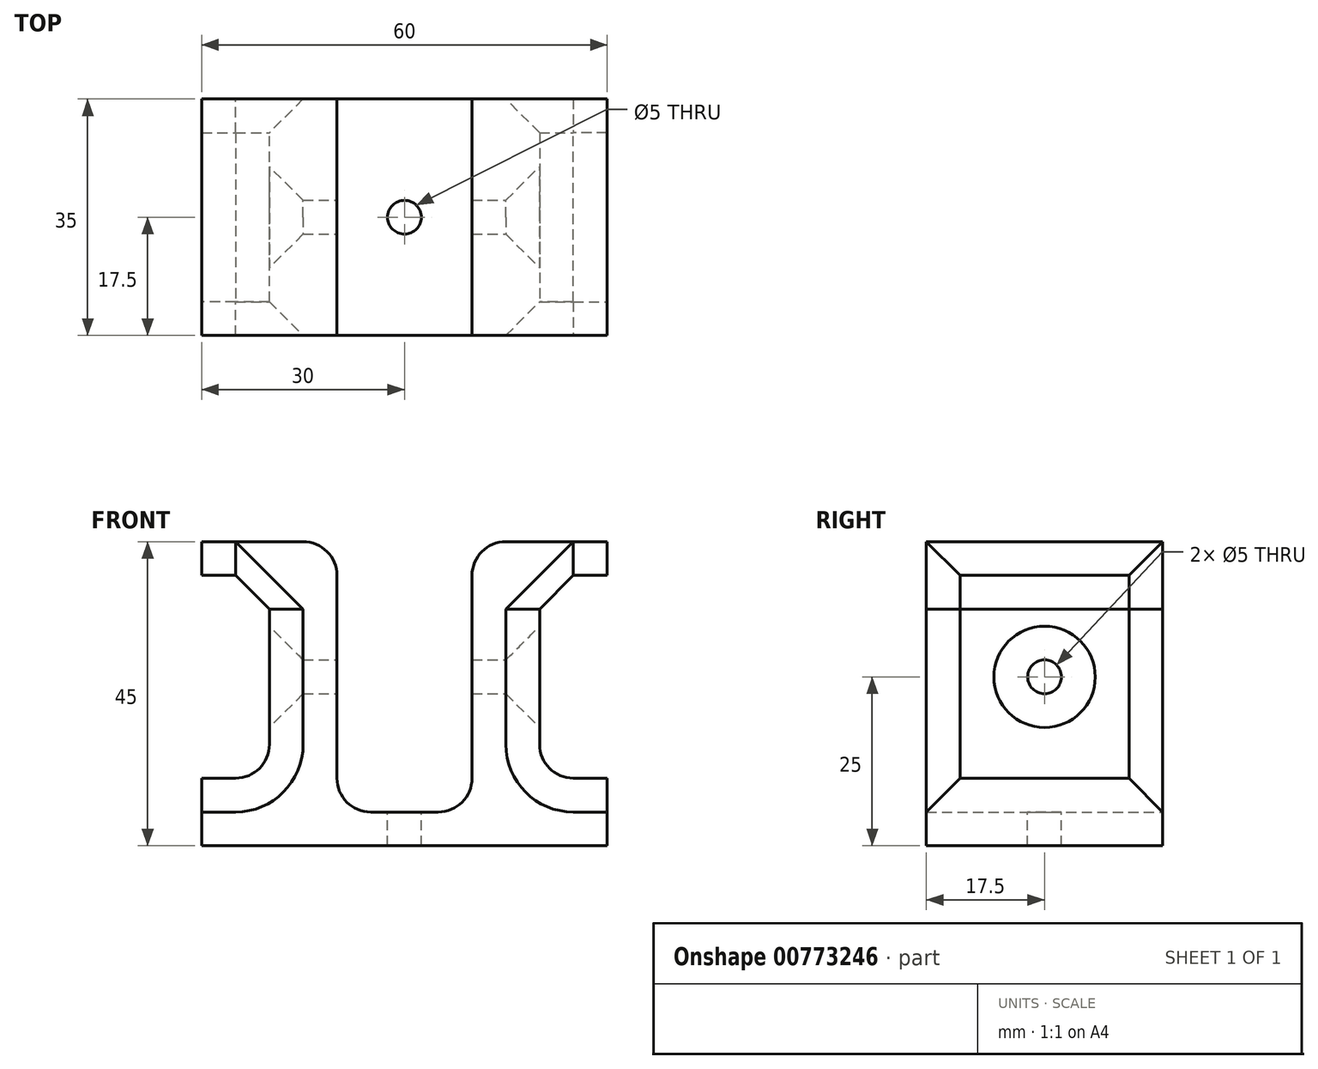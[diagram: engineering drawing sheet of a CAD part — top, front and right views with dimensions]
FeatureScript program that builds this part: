
annotation { "Feature Type Name" : "Feature", "Feature Type Description" : "" }
export const myFeature = defineFeature(function(context is Context, id is Id, definition is map)
    precondition{}
    {
        {
            var Q0;
            Q0=qCreatedBy(makeId("Front.planeOp"),FACE);
            var sketch = newSketch(context, id + "F0", { "sketchPlane" : qUnion([Q0])});
            skLineSegment(sketch, "E0", {"start": v(0, 0) * mm, "end": v(-30, 0) * mm});
            skLineSegment(sketch, "E1", {"start": v(-30, 0) * mm, "end": v(-30, 10) * mm});
            skLineSegment(sketch, "E2", {"start": v(-30, 10) * mm, "end": v(-20, 10) * mm});
            skLineSegment(sketch, "E3", {"start": v(-20, 10) * mm, "end": v(-20, 40) * mm});
            skLineSegment(sketch, "E4", {"start": v(-20, 40) * mm, "end": v(-30, 40) * mm});
            skLineSegment(sketch, "E5", {"start": v(-30, 40) * mm, "end": v(-30, 45) * mm});
            skLineSegment(sketch, "E6", {"start": v(-30, 45) * mm, "end": v(-10, 45) * mm});
            skLineSegment(sketch, "E7", {"start": v(-10, 45) * mm, "end": v(-10, 5) * mm});
            skLineSegment(sketch, "E8", {"start": v(-10, 5) * mm, "end": v(0, 5) * mm});
            skLineSegment(sketch, "E9", {"start": v(0, -15.18) * mm, "end": v(0, 57.22) * mm, "construction": true});
            skLineSegment(sketch, "E10.MirrorCS", {"start": v(30, 0) * mm, "end": v(30, 10) * mm});
            skLineSegment(sketch, "E11.MirrorCS", {"start": v(30, 10) * mm, "end": v(20, 10) * mm});
            skLineSegment(sketch, "E12.MirrorCS", {"start": v(10, 5) * mm, "end": v(0, 5) * mm});
            skLineSegment(sketch, "E13.MirrorCS", {"start": v(10, 45) * mm, "end": v(10, 5) * mm});
            skLineSegment(sketch, "E14.MirrorCS", {"start": v(30, 45) * mm, "end": v(10, 45) * mm});
            skLineSegment(sketch, "E15.MirrorCS", {"start": v(30, 40) * mm, "end": v(30, 45) * mm});
            skLineSegment(sketch, "E16.MirrorCS", {"start": v(0, 0) * mm, "end": v(30, 0) * mm});
            skLineSegment(sketch, "E17.MirrorCS", {"start": v(20, 10) * mm, "end": v(20, 40) * mm});
            skLineSegment(sketch, "E18.MirrorCS", {"start": v(20, 40) * mm, "end": v(30, 40) * mm});
            skSolve(sketch);
        }
        {
            var Q0;
            Q0=makeQuery(id+"F0.imprint","IMPRINT",FACE,{"disambiguationData":[TD([[makeQuery(id+"F0.imprint","IMPRINT",EDGE,{"derivedFrom":sQuery(id+"F0.wireOp",EDGE,"E0")}),-1.0]])]});
            extrude(context, id + "F1", {"entities" : qUnion([Q0]), "endBound" : BoundingType.SYMMETRIC, "depth" : 35 * mm, "offsetDistance" : 25 * mm});
        }
        {
            var Q0;
            Q0=makeQuery(id+"F1.opExtrude","SWEPT_EDGE",EDGE,{"disambiguationData":[OSD([sQuery(id+"F0.wireOp",EDGE,"E11.MirrorCS"),sQuery(id+"F0.wireOp",EDGE,"E17.MirrorCS")])]});
            fillet(context, id + "F2", {"entities" : qUnion([Q0]), "radius" : 5 * mm, "tangentPropagation" : true, "allowEdgeOverflow" : false});
        }
        {
            var Q0;
            Q0=makeQuery(id+"F1.opExtrude","SWEPT_EDGE",EDGE,{"disambiguationData":[OSD([sQuery(id+"F0.wireOp",EDGE,"E2"),sQuery(id+"F0.wireOp",EDGE,"E3")])]});
            fillet(context, id + "F3", {"entities" : qUnion([Q0]), "radius" : 5 * mm, "tangentPropagation" : true, "allowEdgeOverflow" : false});
        }
        {
            var Q0;
            Q0=makeQuery(id+"F1.opExtrude","SWEPT_FACE",FACE,{"disambiguationData":[OSD([sQuery(id+"F0.wireOp",EDGE,"E8"),sQuery(id+"F0.wireOp",EDGE,"E12.MirrorCS")])]});
            var sketch = newSketch(context, id + "F4", { "sketchPlane" : qUnion([Q0])});
            skCircle(sketch, "E19", {"center": v(0, 0) * mm, "radius": 2.5 * mm});
            skSolve(sketch);
        }
        {
            var Q0;
            Q0=makeQuery(id+"F4.imprint","IMPRINT",FACE,{"disambiguationData":[TD([[makeQuery(id+"F4.imprint","IMPRINT",EDGE,{"derivedFrom":sQuery(id+"F4.wireOp",EDGE,"E19")}),1.0]])]});
            extrude(context, id + "F5", {"entities" : qUnion([Q0]), "operationType" : NewBodyOperationType.REMOVE, "oppositeDirection" : true, "depth" : 25 * mm, "offsetDistance" : 25 * mm});
        }
        {
            var Q0;
            Q0=makeQuery(id+"F1.opExtrude","SWEPT_FACE",FACE,{"disambiguationData":[OSD([sQuery(id+"F0.wireOp",EDGE,"E3")])]});
            var Q1;
            Q1=makeQuery(id+"F1.opExtrude","SWEPT_FACE",FACE,{"disambiguationData":[OSD([sQuery(id+"F0.wireOp",EDGE,"E17.MirrorCS")])]});
            chamfer(context, id + "F6", {"entities" : qUnion([Q0, Q1]), "width" : 5 * mm, "tangentPropagation" : true});
        }
        {
            var Q0;
            Q0=makeQuery(id+"F1.opExtrude","SWEPT_EDGE",EDGE,{"disambiguationData":[OSD([sQuery(id+"F0.wireOp",EDGE,"E7"),sQuery(id+"F0.wireOp",EDGE,"E8")])]});
            var Q1;
            Q1=makeQuery(id+"F1.opExtrude","SWEPT_EDGE",EDGE,{"disambiguationData":[OSD([sQuery(id+"F0.wireOp",EDGE,"E12.MirrorCS"),sQuery(id+"F0.wireOp",EDGE,"E13.MirrorCS")])]});
            var Q2;
            Q2=makeQuery(id+"F1.opExtrude","SWEPT_EDGE",EDGE,{"disambiguationData":[OSD([sQuery(id+"F0.wireOp",EDGE,"E6"),sQuery(id+"F0.wireOp",EDGE,"E7")])]});
            var Q3;
            Q3=makeQuery(id+"F1.opExtrude","SWEPT_EDGE",EDGE,{"disambiguationData":[OSD([sQuery(id+"F0.wireOp",EDGE,"E13.MirrorCS"),sQuery(id+"F0.wireOp",EDGE,"E14.MirrorCS")])]});
            fillet(context, id + "F7", {"entities" : qUnion([Q0, Q1, Q2, Q3]), "radius" : 5 * mm, "tangentPropagation" : true, "allowEdgeOverflow" : false});
        }
        {
            var Q0;
            Q0=qCreatedBy(makeId("Right.planeOp"),FACE);
            var sketch = newSketch(context, id + "F8", { "sketchPlane" : qUnion([Q0])});
            skCircle(sketch, "E20", {"center": v(0, 25) * mm, "radius": 2.5 * mm});
            skSolve(sketch);
        }
        {
            var Q0;
            Q0=makeQuery(id+"F8.imprint","IMPRINT",FACE,{"disambiguationData":[TD([[makeQuery(id+"F8.imprint","IMPRINT",EDGE,{"derivedFrom":sQuery(id+"F8.wireOp",EDGE,"E20")}),1.0]])]});
            var Q1;
            Q1 = qSketchRegion(id + "F8", true);
            extrude(context, id + "F9", {"entities" : qUnion([Q0, Q1]), "operationType" : NewBodyOperationType.REMOVE, "oppositeDirection" : true, "depth" : 25 * mm, "offsetDistance" : 25 * mm, "hasSecondDirection" : true, "secondDirectionOppositeDirection" : false, "secondDirectionDepth" : 25 * mm});
        }
        {
            var Q0;
            Q0=makeQuery(id+"F9.boolean.opBoolean","INTERSECT",EDGE,{"derivedFrom":[makeQuery(id+"F1.opExtrude","SWEPT_FACE",FACE,{"disambiguationData":[OSD([sQuery(id+"F0.wireOp",EDGE,"E3")])]}),makeQuery(id+"F9.opExtrude","SWEPT_FACE",FACE,{"disambiguationData":[OSD([sQuery(id+"F8.wireOp",EDGE,"E20")])]})]});
            var Q1;
            Q1=makeQuery(id+"F9.boolean.opBoolean","INTERSECT",EDGE,{"derivedFrom":[makeQuery(id+"F1.opExtrude","SWEPT_FACE",FACE,{"disambiguationData":[OSD([sQuery(id+"F0.wireOp",EDGE,"E17.MirrorCS")])]}),makeQuery(id+"F9.opExtrude","SWEPT_FACE",FACE,{"disambiguationData":[OSD([sQuery(id+"F8.wireOp",EDGE,"E20")])]})]});
            chamfer(context, id + "F10", {"entities" : qUnion([Q0, Q1]), "width" : 5 * mm, "tangentPropagation" : true});
        }
    });
